# Revit family: 63_UN_Recessed_Small Island_Signify
name_source: partatom
category: Lighting Fixtures
units: mm (PartAtom-declared; Revit-internal decimal feet)

## family parameters
Always vertical = Yes
Cut with Voids When Loaded = No
Light Source = No
OmniClass Number = 23.80.70.11.14.11
OmniClass Title = Downlights
Part Type = Normal
Room Calculation Point = Yes
Round Connector Dimension = Use Diameter
Shared = No
Work Plane-Based = No

## types (1)
- NC Skylight W60L60_Day Rhythm_Noon start
    Apparent Load = 40 VA
    Assembly Code = 63.0
    Calc_L1_Symbol = 6 mm  [stored 0.019685 ft]
    Calc_L2_Symbol = 6 mm  [stored 0.019685 ft]
    Description = https://www.signify.com
    ETIM Code = ETIMCODE
    GTIN Code = GTINCODE
    Glass_Material = Glass, SkyColor, High Luminance
    Housing_Material = Laminate, White
    IK Value = -
    IP Value = -
    ISBN Code = ISBNCODE
    IfcExportAs = IfcLightFixtureType
    IfcExportType = USERDEFINED
    Lamp = LED
    Luminous Flux (lm) = 2505 lm
    Manufacturer = Signify - NatureConnect
    Model = Small Island
    Type Comments = Small Island
    URL = https://www.ivlibrary.com
    Voltage = 230 V
    Wattage Comments = -

note: [stored X ft] marks values corroborated as IEEE doubles in the binary element streams (Revit-internal decimal feet)

## geometry (parser evidence)
native form markers: Sweep x10
no freeform markers — native parametric forms only
